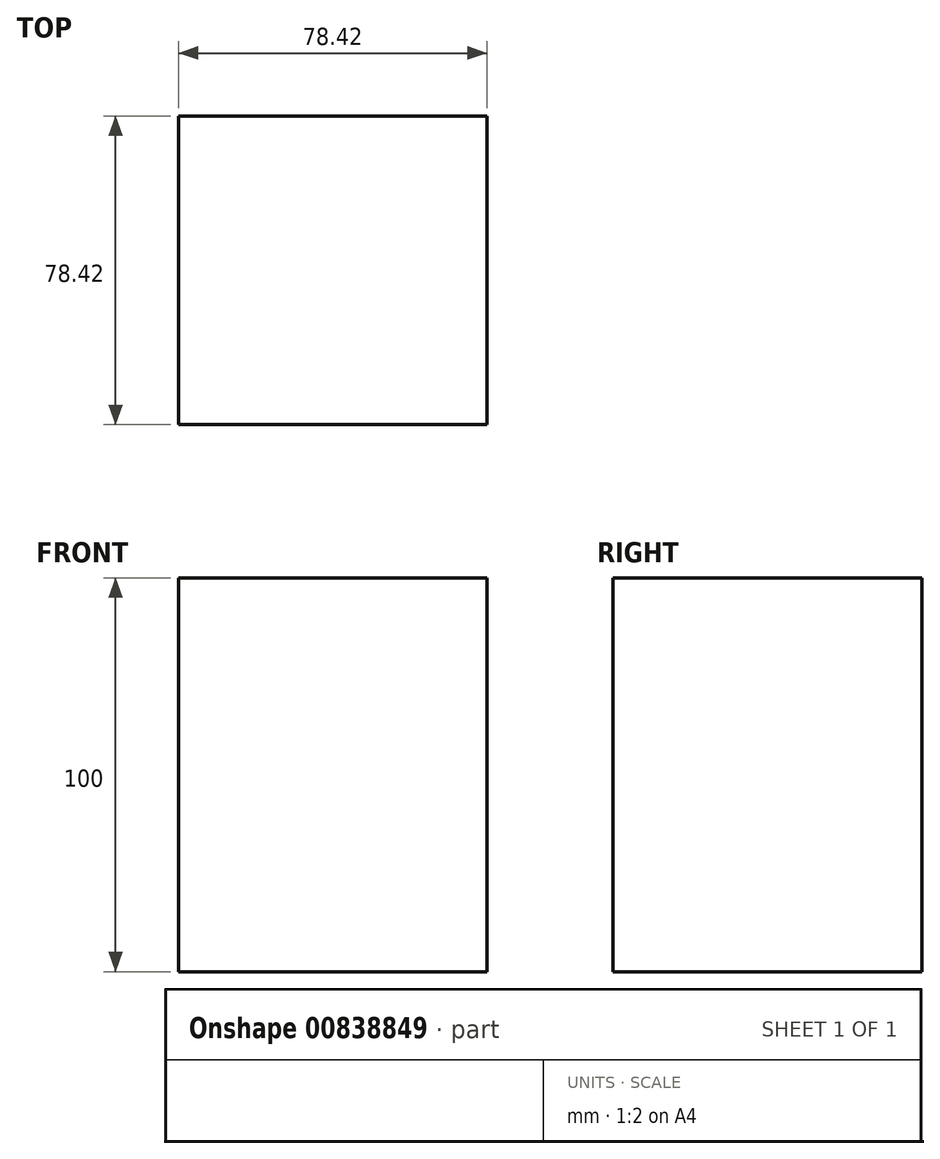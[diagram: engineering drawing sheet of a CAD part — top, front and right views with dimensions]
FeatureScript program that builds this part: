
annotation { "Feature Type Name" : "Feature", "Feature Type Description" : "" }
export const myFeature = defineFeature(function(context is Context, id is Id, definition is map)
    precondition{}
    {
        {
            var Q0;
            Q0=qCreatedBy(makeId("Top.planeOp"),FACE);
            var sketch = newSketch(context, id + "F0", { "sketchPlane" : qUnion([Q0])});
            skLineSegment(sketch, "E0.bottom", {"start": v(39.21, 39.21) * mm, "end": v(-39.21, 39.21) * mm});
            skLineSegment(sketch, "E0.top", {"start": v(39.21, -39.21) * mm, "end": v(-39.21, -39.21) * mm});
            skLineSegment(sketch, "E0.left", {"start": v(39.21, 39.21) * mm, "end": v(39.21, -39.21) * mm});
            skLineSegment(sketch, "E0.right", {"start": v(-39.21, 39.21) * mm, "end": v(-39.21, -39.21) * mm});
            skPoint(sketch, "E0.middle", {"position": v(0, 0) * mm});
            skSolve(sketch);
        }
        {
            var Q0;
            Q0 = qSketchRegion(id + "F0", true);
            extrude(context, id + "F1", {"entities" : qUnion([Q0]), "depth" : 100 * mm, "offsetDistance" : 25 * mm});
        }
    });
